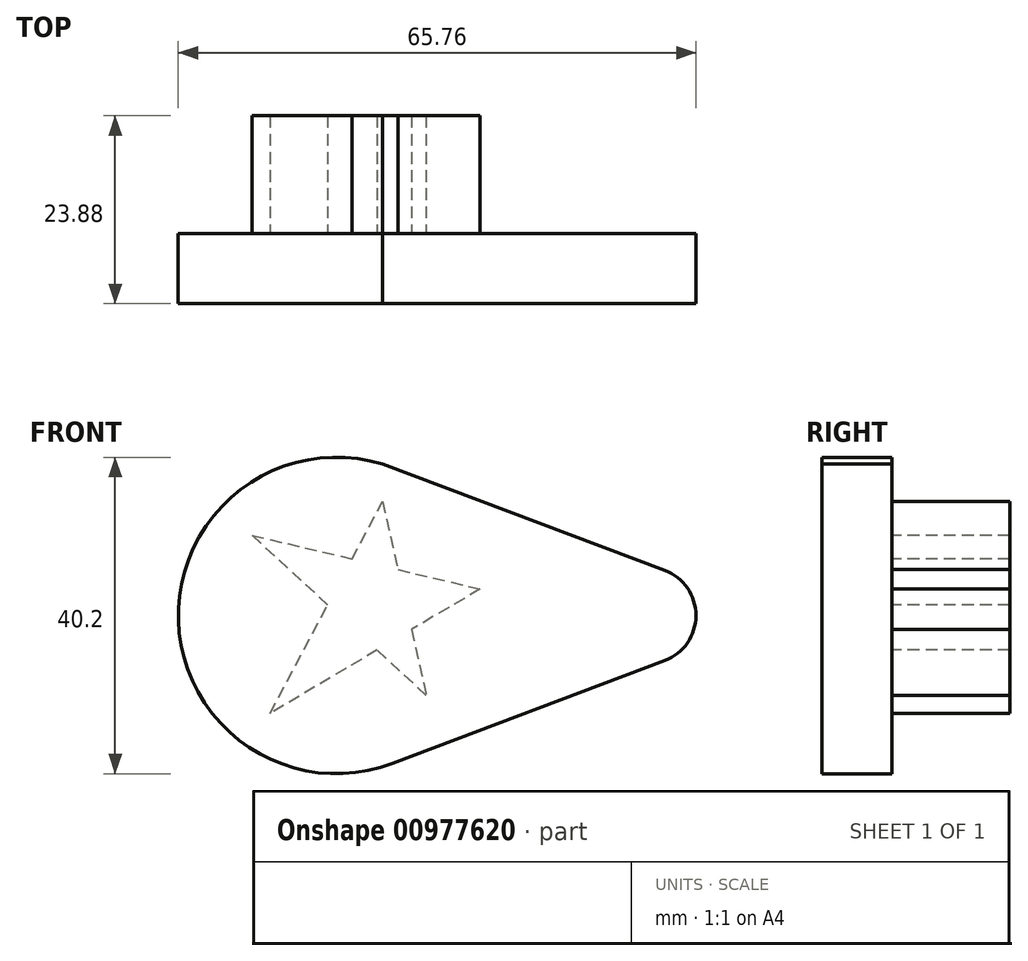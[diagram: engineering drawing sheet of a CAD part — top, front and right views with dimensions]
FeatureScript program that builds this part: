
annotation { "Feature Type Name" : "Feature", "Feature Type Description" : "" }
export const myFeature = defineFeature(function(context is Context, id is Id, definition is map)
    precondition{}
    {
        {
            var Q0;
            Q0=qCreatedBy(makeId("Front.planeOp"),FACE);
            var sketch = newSketch(context, id + "F0", { "sketchPlane" : qUnion([Q0])});
            skCircle(sketch, "E0", {"center": v(0, 0) * mm, "radius": 20.1 * mm});
            skCircle(sketch, "E1", {"center": v(39.55, 0) * mm, "radius": 6.1 * mm});
            skLineSegment(sketch, "E2", {"start": v(5.86, 19.23) * mm, "end": v(41.7, 5.71) * mm});
            skLineSegment(sketch, "E3", {"start": v(41.7, 5.71) * mm, "end": v(41.7, -5.71) * mm});
            skLineSegment(sketch, "E4", {"start": v(41.7, -5.71) * mm, "end": v(7.11, -18.8) * mm});
            skSolve(sketch);
        }
        {
            var Q0;
            {var subQ0=sQuery(id+"F0.wireOp",EDGE,"E2");var subQ1=sQuery(id+"F0.wireOp",EDGE,"E0");var subQ2=makeQuery(id+"F0.imprint","INTERSECT",VERTEX,{"disambiguationData":[OD(0.0)],"derivedFrom":[subQ1,subQ0]});Q0=makeQuery(id+"F0.imprint","IMPRINT",FACE,{"disambiguationData":[TD([[makeQuery(id+"F0.imprint","IMPRINT",EDGE,{"disambiguationData":[TD([[subQ2,-1.0]])],"derivedFrom":subQ1}),1.0]])]});}
            var Q1;
            {var subQ0=sQuery(id+"F0.wireOp",EDGE,"E4");Q1=makeQuery(id+"F0.imprint","IMPRINT",FACE,{"disambiguationData":[TD([[makeQuery(id+"F0.imprint","IMPRINT",EDGE,{"derivedFrom":subQ0}),-1.0]])]});}
            var Q2;
            {var subQ0=sQuery(id+"F0.wireOp",EDGE,"E3");Q2=makeQuery(id+"F0.imprint","IMPRINT",FACE,{"disambiguationData":[TD([[makeQuery(id+"F0.imprint","IMPRINT",EDGE,{"derivedFrom":subQ0}),-1.0]])]});}
            var Q3;
            {var subQ0=sQuery(id+"F0.wireOp",EDGE,"E3");Q3=makeQuery(id+"F0.imprint","IMPRINT",FACE,{"disambiguationData":[TD([[makeQuery(id+"F0.imprint","IMPRINT",EDGE,{"derivedFrom":subQ0}),1.0]])]});}
            extrude(context, id + "F1", {"entities" : qUnion([Q0, Q1, Q2, Q3]), "depth" : 8.9 * mm, "offsetDistance" : 25.4 * mm});
        }
        {
            var Q0;
            Q0=makeQuery(id+"F1.opExtrude","CAP_FACE",FACE,{"disambiguationData":[OSD([sQuery(id+"F0.wireOp",EDGE,"E0"),sQuery(id+"F0.wireOp",EDGE,"E1"),sQuery(id+"F0.wireOp",EDGE,"E2"),sQuery(id+"F0.wireOp",EDGE,"E4")])],"isStart":false});
            var sketch = newSketch(context, id + "F2", { "sketchPlane" : qUnion([Q0])});
            skLineSegment(sketch, "E5", {"start": v(-10.7, 10.18) * mm, "end": v(18.22, 3.37) * mm});
            skLineSegment(sketch, "E6", {"start": v(18.22, 3.37) * mm, "end": v(-8.43, -12.44) * mm});
            skLineSegment(sketch, "E7", {"start": v(-8.43, -12.44) * mm, "end": v(5.86, 14.5) * mm});
            skLineSegment(sketch, "E8", {"start": v(5.86, 14.5) * mm, "end": v(11.4, -10.16) * mm});
            skLineSegment(sketch, "E9", {"start": v(11.4, -10.16) * mm, "end": v(-10.7, 10.18) * mm});
            skSolve(sketch);
        }
        {
            var Q0;
            {var subQ0=sQuery(id+"F2.wireOp",EDGE,"E7");var subQ1=sQuery(id+"F2.wireOp",EDGE,"E5");var subQ2=makeQuery(id+"F2.imprint","INTERSECT",VERTEX,{"derivedFrom":[subQ1,subQ0]});Q0=makeQuery(id+"F2.imprint","IMPRINT",FACE,{"disambiguationData":[TD([[makeQuery(id+"F2.imprint","IMPRINT",EDGE,{"disambiguationData":[TD([[subQ2,-1.0]])],"derivedFrom":subQ1}),1.0]])]});}
            var Q1;
            {var subQ1=sQuery(id+"F2.wireOp",EDGE,"E5");var subQ5=sQuery(id+"F2.wireOp",EDGE,"E7");var subQ6=makeQuery(id+"F2.imprint","INTERSECT",VERTEX,{"derivedFrom":[subQ1,subQ5]});Q1=makeQuery(id+"F2.imprint","IMPRINT",FACE,{"disambiguationData":[TD([[makeQuery(id+"F2.imprint","IMPRINT",EDGE,{"disambiguationData":[TD([[subQ6,-1.0]])],"derivedFrom":subQ1}),-1.0]])]});}
            var Q2;
            {var subQ0=sQuery(id+"F2.wireOp",EDGE,"E9");var subQ1=sQuery(id+"F2.wireOp",EDGE,"E5");var subQ2=makeQuery(id+"F2.imprint","INTERSECT",VERTEX,{"derivedFrom":[subQ1,subQ0]});Q2=makeQuery(id+"F2.imprint","IMPRINT",FACE,{"disambiguationData":[TD([[makeQuery(id+"F2.imprint","IMPRINT",EDGE,{"disambiguationData":[TD([[subQ2,-1.0]])],"derivedFrom":subQ1}),-1.0]])]});}
            var Q3;
            {var subQ0=sQuery(id+"F2.wireOp",EDGE,"E7");var subQ1=sQuery(id+"F2.wireOp",EDGE,"E6");var subQ2=makeQuery(id+"F2.imprint","INTERSECT",VERTEX,{"derivedFrom":[subQ1,subQ0]});Q3=makeQuery(id+"F2.imprint","IMPRINT",FACE,{"disambiguationData":[TD([[makeQuery(id+"F2.imprint","IMPRINT",EDGE,{"disambiguationData":[TD([[subQ2,1.0]])],"derivedFrom":subQ1}),-1.0]])]});}
            var Q4;
            {var subQ0=sQuery(id+"F2.wireOp",EDGE,"E8");var subQ1=sQuery(id+"F2.wireOp",EDGE,"E6");var subQ2=makeQuery(id+"F2.imprint","INTERSECT",VERTEX,{"derivedFrom":[subQ1,subQ0]});Q4=makeQuery(id+"F2.imprint","IMPRINT",FACE,{"disambiguationData":[TD([[makeQuery(id+"F2.imprint","IMPRINT",EDGE,{"disambiguationData":[TD([[subQ2,-1.0]])],"derivedFrom":subQ1}),1.0]])]});}
            var Q5;
            {var subQ0=sQuery(id+"F2.wireOp",EDGE,"E6");var subQ1=sQuery(id+"F2.wireOp",EDGE,"E5");var subQ2=makeQuery(id+"F2.imprint","INTERSECT",VERTEX,{"derivedFrom":[subQ1,subQ0]});Q5=makeQuery(id+"F2.imprint","IMPRINT",FACE,{"disambiguationData":[TD([[makeQuery(id+"F2.imprint","IMPRINT",EDGE,{"disambiguationData":[TD([[subQ2,1.0]])],"derivedFrom":subQ1}),-1.0]])]});}
            extrude(context, id + "F3", {"entities" : qUnion([Q0, Q1, Q2, Q3, Q4, Q5]), "operationType" : NewBodyOperationType.ADD, "oppositeDirection" : true, "depth" : 23.88 * mm, "offsetDistance" : 25.4 * mm});
        }
    });
